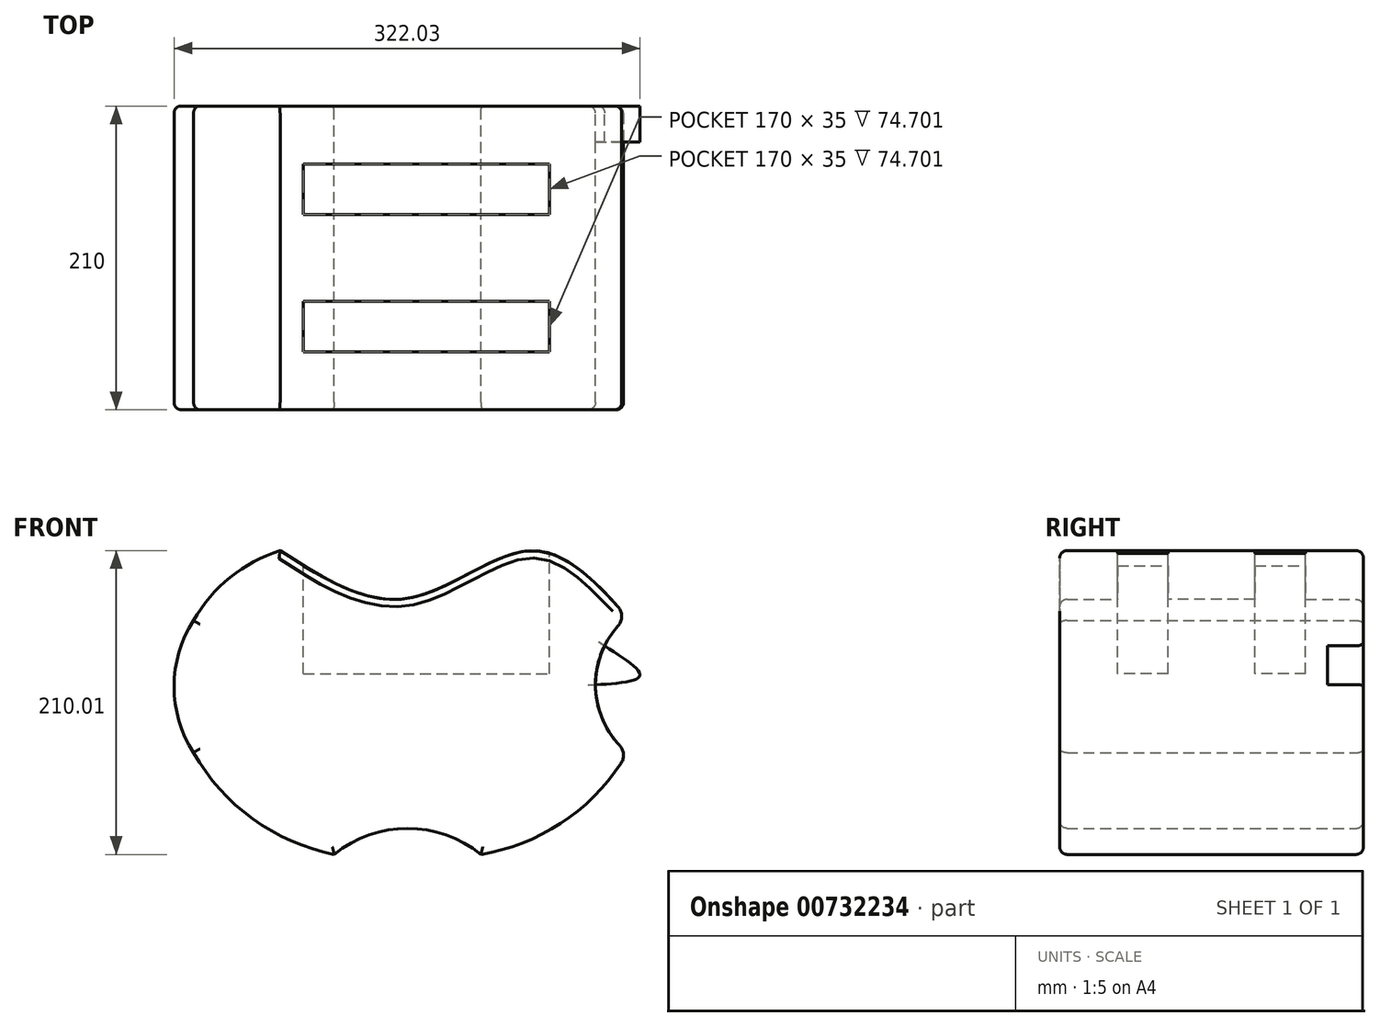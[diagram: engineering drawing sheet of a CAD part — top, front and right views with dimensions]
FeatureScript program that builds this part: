
annotation { "Feature Type Name" : "Feature", "Feature Type Description" : "" }
export const myFeature = defineFeature(function(context is Context, id is Id, definition is map)
    precondition{}
    {
        {
            var Q0;
            Q0=qCreatedBy(makeId("Front.planeOp"),FACE);
            var sketch = newSketch(context, id + "F0", { "sketchPlane" : qUnion([Q0])});
            skArc(sketch, "E0", {"start": v(0, 70.39) * mm, "mid": v(40.95, 24.57) * mm, "end": v(97.27, 0) * mm});
            skArc(sketch, "E1", {"start": v(198.64, 0) * mm, "mid": v(257.24, 23.78) * mm, "end": v(300, 70.39) * mm});
            skArc(sketch, "E2", {"start": v(198.64, 0) * mm, "mid": v(147.95, 18.06) * mm, "end": v(97.27, 0) * mm});
            skArc(sketch, "E3", {"start": v(0, 161.74) * mm, "mid": v(-13.47, 116.07) * mm, "end": v(0, 70.39) * mm});
            skArc(sketch, "E4", {"start": v(59.83, 210) * mm, "mid": v(25.28, 191.62) * mm, "end": v(0, 161.74) * mm});
            skArc(sketch, "E5", {"start": v(300, 164.12) * mm, "mid": v(277.83, 117.25) * mm, "end": v(300, 70.39) * mm});
            skPoint(sketch, "E6.1.internal.snap0", {"position": v(147.95, 18.06) * mm});
            skFitSpline(sketch, "E6", {"points": [v(59.83, 210) * mm, v(147.95, 177.04) * mm, v(233.45, 210) * mm, v(300, 164.12) * mm], "startDerivative": vector(254.94, -164.78) * mm, "endDerivative": vector(198.3, -219.15) * mm});
            skLineSegment(sketch, "E7", {"start": v(147.95, 177.04) * mm, "end": v(147.95, 18.06) * mm, "construction": true});
            skLineSegment(sketch, "E8", {"start": v(-13.47, 117.25) * mm, "end": v(277.83, 117.25) * mm, "construction": true});
            skPoint(sketch, "E8.startSnap0", {"position": v(277.83, 117.25) * mm});
            skFitSpline(sketch, "E9", {"points": [v(277.83, 117.25) * mm, v(308.49, 123.58) * mm, v(284.16, 144.23) * mm], "startDerivative": vector(86.37, 6.11) * mm, "endDerivative": vector(-73.47, 47.53) * mm});
            skSolve(sketch);
        }
        {
            var Q0;
            Q0=makeQuery(id+"F0.imprint","IMPRINT",FACE,{"disambiguationData":[TD([[makeQuery(id+"F0.imprint","IMPRINT",EDGE,{"derivedFrom":sQuery(id+"F0.wireOp",EDGE,"E0")}),1.0]])]});
            var Q1;
            {var subQ0=sQuery(id+"F0.wireOp",EDGE,"HS6DrHtl-vWuy-QQOv-Bg2y-yJfrd3j6cq9S");Q1=makeQuery(id+"F0.imprint","IMPRINT",FACE,{"disambiguationData":[TD([[makeQuery(id+"F0.imprint","IMPRINT",EDGE,{"derivedFrom":subQ0}),-1.0]])]});}
            extrude(context, id + "F1", {"entities" : qUnion([Q0, Q1]), "depth" : 210 * mm, "offsetDistance" : 25 * mm});
        }
        {
            var Q0;
            Q0 = qSketchRegion(id + "F0", true);
            extrude(context, id + "F2", {"entities" : qUnion([Q0]), "operationType" : NewBodyOperationType.ADD, "depth" : 25 * mm, "offsetDistance" : 25 * mm});
        }
        {
            var Q0;
            Q0=makeQuery(id+"F1.opExtrude","CAP_EDGE",EDGE,{"disambiguationData":[OSD([sQuery(id+"F0.wireOp",EDGE,"E6")])],"isStart":true});
            var Q1;
            Q1=makeQuery(id+"F1.opExtrude","CAP_EDGE",EDGE,{"disambiguationData":[OSD([sQuery(id+"F0.wireOp",EDGE,"E4")])],"isStart":true});
            var Q2;
            Q2=makeQuery(id+"F1.opExtrude","CAP_EDGE",EDGE,{"disambiguationData":[OSD([sQuery(id+"F0.wireOp",EDGE,"E3")])],"isStart":true});
            var Q3;
            Q3=makeQuery(id+"F1.opExtrude","CAP_EDGE",EDGE,{"disambiguationData":[OSD([sQuery(id+"F0.wireOp",EDGE,"E0")])],"isStart":true});
            var Q4;
            Q4=makeQuery(id+"F1.opExtrude","CAP_EDGE",EDGE,{"disambiguationData":[OSD([sQuery(id+"F0.wireOp",EDGE,"E2")])],"isStart":true});
            var Q5;
            Q5=makeQuery(id+"F1.opExtrude","CAP_EDGE",EDGE,{"disambiguationData":[OSD([sQuery(id+"F0.wireOp",EDGE,"E1")])],"isStart":true});
            var Q6;
            {var subQ0=sQuery(id+"F0.wireOp",EDGE,"E5");Q6=makeQuery(id+"F1.opExtrude","CAP_EDGE",EDGE,{"disambiguationData":[OSD([subQ0]),TDD([makeQuery(id+"F0.imprint","IMPRINT",EDGE,{"disambiguationData":[TD([[makeQuery(id+"F0.imprint","INTERSECT",VERTEX,{"derivedFrom":[sQuery(id+"F0.wireOp",EDGE,"E1"),subQ0]}),1.0]])],"derivedFrom":subQ0})])],"isStart":true});}
            var Q7;
            {var subQ0=sQuery(id+"F0.wireOp",EDGE,"E5");Q7=makeQuery(id+"F1.opExtrude","CAP_EDGE",EDGE,{"disambiguationData":[OSD([subQ0]),TDD([makeQuery(id+"F0.imprint","IMPRINT",EDGE,{"disambiguationData":[TD([[makeQuery(id+"F0.imprint","INTERSECT",VERTEX,{"derivedFrom":[subQ0,sQuery(id+"F0.wireOp",EDGE,"E6")]}),-1.0]])],"derivedFrom":subQ0})])],"isStart":true});}
            fillet(context, id + "F3", {"entities" : qUnion([Q0, Q1, Q2, Q3, Q4, Q5, Q6, Q7]), "radius" : 5 * mm, "tangentPropagation" : true, "allowEdgeOverflow" : false});
        }
        {
            var Q0;
            Q0=makeQuery(id+"F1.opExtrude","CAP_EDGE",EDGE,{"disambiguationData":[OSD([sQuery(id+"F0.wireOp",EDGE,"E6")])],"isStart":false});
            var Q1;
            Q1=makeQuery(id+"F1.opExtrude","CAP_EDGE",EDGE,{"disambiguationData":[OSD([sQuery(id+"F0.wireOp",EDGE,"E4")])],"isStart":false});
            var Q2;
            Q2=makeQuery(id+"F1.opExtrude","CAP_EDGE",EDGE,{"disambiguationData":[OSD([sQuery(id+"F0.wireOp",EDGE,"E3")])],"isStart":false});
            var Q3;
            Q3=makeQuery(id+"F1.opExtrude","CAP_EDGE",EDGE,{"disambiguationData":[OSD([sQuery(id+"F0.wireOp",EDGE,"E0")])],"isStart":false});
            var Q4;
            Q4=makeQuery(id+"F1.opExtrude","CAP_EDGE",EDGE,{"disambiguationData":[OSD([sQuery(id+"F0.wireOp",EDGE,"E2")])],"isStart":false});
            var Q5;
            Q5=makeQuery(id+"F1.opExtrude","CAP_EDGE",EDGE,{"disambiguationData":[OSD([sQuery(id+"F0.wireOp",EDGE,"E1")])],"isStart":false});
            var Q6;
            {var subQ0=sQuery(id+"F0.wireOp",EDGE,"E5");Q6=makeQuery(id+"F1.opExtrude","CAP_EDGE",EDGE,{"disambiguationData":[OSD([subQ0]),TDD([makeQuery(id+"F0.imprint","IMPRINT",EDGE,{"disambiguationData":[TD([[makeQuery(id+"F0.imprint","INTERSECT",VERTEX,{"derivedFrom":[sQuery(id+"F0.wireOp",EDGE,"E1"),subQ0]}),1.0]])],"derivedFrom":subQ0})])],"isStart":false});}
            var Q7;
            {var subQ0=sQuery(id+"F0.wireOp",EDGE,"E5");Q7=makeQuery(id+"F1.opExtrude","CAP_EDGE",EDGE,{"disambiguationData":[OSD([subQ0]),TDD([makeQuery(id+"F0.imprint","IMPRINT",EDGE,{"disambiguationData":[TD([[makeQuery(id+"F0.imprint","INTERSECT",VERTEX,{"derivedFrom":[subQ0,sQuery(id+"F0.wireOp",EDGE,"E6")]}),-1.0]])],"derivedFrom":subQ0})])],"isStart":false});}
            fillet(context, id + "F4", {"entities" : qUnion([Q0, Q1, Q2, Q3, Q4, Q5, Q6, Q7]), "radius" : 5 * mm, "tangentPropagation" : true, "allowEdgeOverflow" : false});
        }
        {
            var Q0;
            Q0=qCreatedBy(makeId("Top.planeOp"),FACE);
            cPlane(context, id + "F5", {"entities" : qUnion([Q0]), "cplaneType" : CPlaneType.OFFSET, "offset" : 225 * mm, "width" : 150 * mm, "height" : 150 * mm});
        }
        {
            var Q0;
            Q0=qCreatedBy(id+"F5.planeOp",FACE);
            var sketch = newSketch(context, id + "F6", { "sketchPlane" : qUnion([Q0])});
            skLineSegment(sketch, "E10", {"start": v(76, -40) * mm, "end": v(76, -75) * mm});
            skLineSegment(sketch, "E11", {"start": v(76, -75) * mm, "end": v(246, -75) * mm});
            skLineSegment(sketch, "E12", {"start": v(246, -75) * mm, "end": v(246, -40) * mm});
            skLineSegment(sketch, "E13", {"start": v(246, -40) * mm, "end": v(76, -40) * mm});
            skLineSegment(sketch, "E14.bottom", {"start": v(76, -135) * mm, "end": v(246, -135) * mm});
            skLineSegment(sketch, "E14.top", {"start": v(76, -170) * mm, "end": v(246, -170) * mm});
            skLineSegment(sketch, "E14.left", {"start": v(76, -135) * mm, "end": v(76, -170) * mm});
            skLineSegment(sketch, "E14.right", {"start": v(246, -135) * mm, "end": v(246, -170) * mm});
            skSolve(sketch);
        }
        {
            var Q0;
            Q0 = qSketchRegion(id + "F6", true);
            extrude(context, id + "F7", {"entities" : qUnion([Q0]), "operationType" : NewBodyOperationType.REMOVE, "oppositeDirection" : true, "depth" : 100 * mm, "offsetDistance" : 25 * mm});
        }
        {
            var Q0;
            Q0=makeQuery(id+"F1.opExtrude","SWEPT_EDGE",EDGE,{"disambiguationData":[OSD([sQuery(id+"F0.wireOp",EDGE,"E5"),sQuery(id+"F0.wireOp",EDGE,"E6")])]});
            var Q1;
            Q1=makeQuery(id+"F1.opExtrude","SWEPT_EDGE",EDGE,{"disambiguationData":[OSD([sQuery(id+"F0.wireOp",EDGE,"E1"),sQuery(id+"F0.wireOp",EDGE,"E5")])]});
            fillet(context, id + "F8", {"entities" : qUnion([Q0, Q1]), "radius" : 10 * mm, "tangentPropagation" : true, "allowEdgeOverflow" : false});
        }
    });
